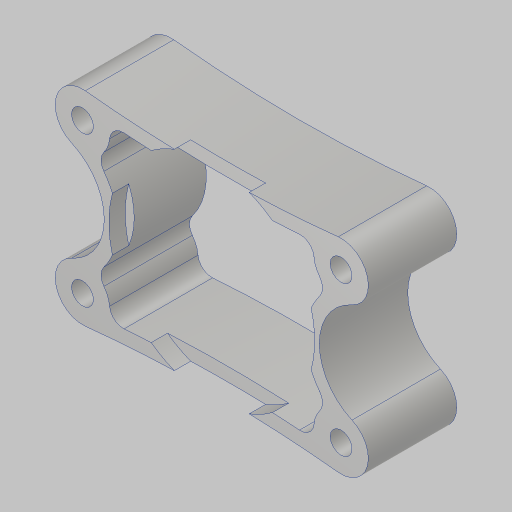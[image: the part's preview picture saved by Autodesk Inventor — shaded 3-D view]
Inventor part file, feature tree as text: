
AUTODESK INVENTOR PART (.ipt)
format: ipt  version: 2023.5 (Build 275446000, 446)  size: 202,752 bytes
history: native  units: in
note: dims shown in document units (in); Inventor stores cm internally (conversion verified against a paired STEP export)
features: sketch x2, extrude x2, fillet x1, hole x1
ambient origin geometry x8: Origin, YZ Plane, XZ Plane, XY Plane, X Axis, Y Axis, Z Axis, Center Point
bodies: Solid1 (feature_tree)
feature tree (6):
  sketch  "Sketch1"  dims[d0=2.375in d1=1.375in d2=0.5in]
  extrude  "Extrusion1"  Depth=0.5in
  fillet  "Fillet1"  Radius=0.5in
  hole  "Hole1"  [1 undecoded]
  extrude  "Extrusion2"  Depth=0.5in
  sketch  "Sketch3"  dims[d3=0.5in d4=0.5in d5=0.5in d6=1.75in d7=0.5in d8=0.5in d9=0.125in d10=0.125in d11=0.812in d12=0.0in d13=0.125in d14=0.201in d15=0.75in d16=0.385in d17=0.25in d18=0.5635in d19=1.0in d20=0.8108in d21=1.89in d22=0.15in d23=0.0in]
note: 1 required parameter value undecoded (feature->parameter linkage not recoverable at this tier; creation-order binding heuristic only, values carry confidence <= 0.55)
